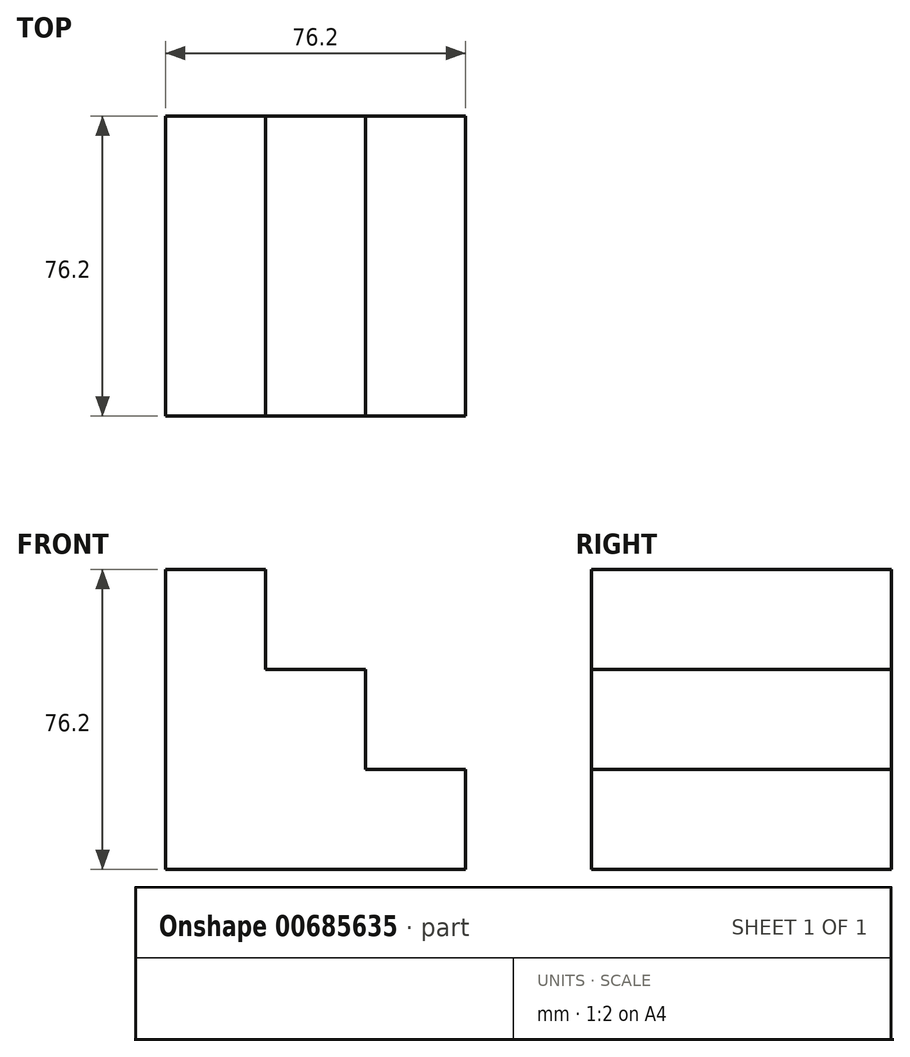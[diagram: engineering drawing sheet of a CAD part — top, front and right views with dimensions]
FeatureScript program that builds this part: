
annotation { "Feature Type Name" : "Feature", "Feature Type Description" : "" }
export const myFeature = defineFeature(function(context is Context, id is Id, definition is map)
    precondition{}
    {
        {
            var Q0;
            Q0=qCreatedBy(makeId("Front.planeOp"),FACE);
            var sketch = newSketch(context, id + "F0", { "sketchPlane" : qUnion([Q0])});
            skLineSegment(sketch, "E0", {"start": v(-49.66, 54.76) * mm, "end": v(-49.66, -21.44) * mm});
            skLineSegment(sketch, "E1", {"start": v(-49.66, -21.44) * mm, "end": v(26.54, -21.44) * mm});
            skLineSegment(sketch, "E2", {"start": v(26.54, -21.44) * mm, "end": v(26.54, 3.96) * mm});
            skLineSegment(sketch, "E3", {"start": v(26.54, 3.96) * mm, "end": v(1.14, 3.96) * mm});
            skLineSegment(sketch, "E4", {"start": v(1.14, 3.96) * mm, "end": v(1.14, 29.36) * mm});
            skLineSegment(sketch, "E5", {"start": v(1.14, 29.36) * mm, "end": v(-24.26, 29.36) * mm});
            skLineSegment(sketch, "E6", {"start": v(-24.26, 29.36) * mm, "end": v(-24.26, 54.76) * mm});
            skLineSegment(sketch, "E7", {"start": v(-24.26, 54.76) * mm, "end": v(-49.66, 54.76) * mm});
            skSolve(sketch);
        }
        {
            var Q0;
            Q0 = qSketchRegion(id + "F0", true);
            extrude(context, id + "F1", {"entities" : qUnion([Q0]), "depth" : 76.2 * mm, "offsetDistance" : 25.4 * mm});
        }
    });
